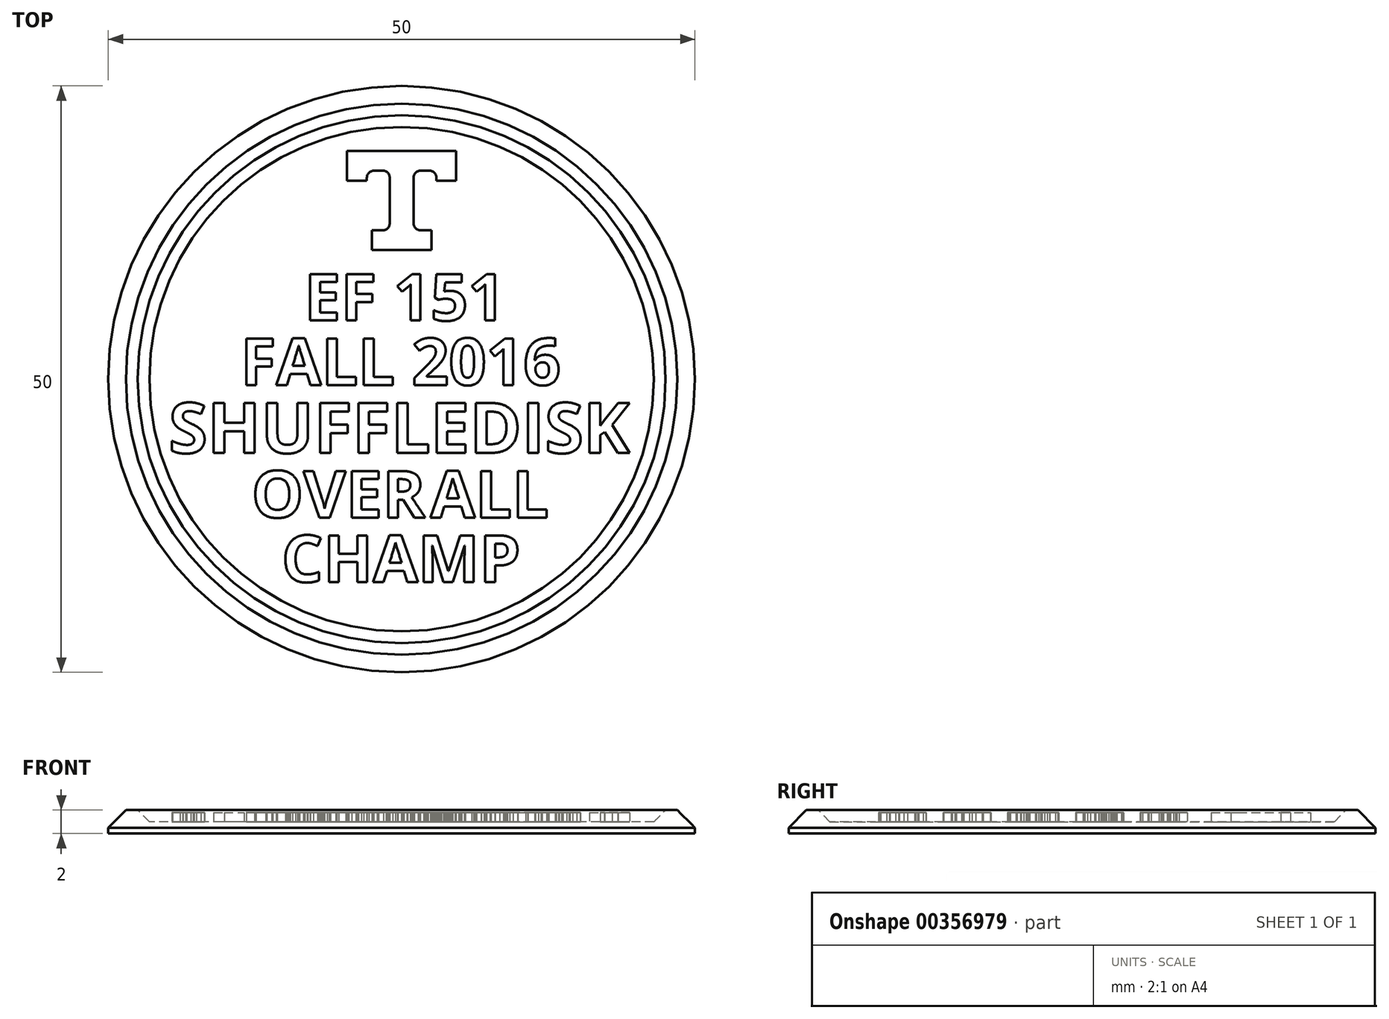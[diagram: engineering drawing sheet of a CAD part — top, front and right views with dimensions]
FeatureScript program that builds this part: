
annotation { "Feature Type Name" : "Feature", "Feature Type Description" : "" }
export const myFeature = defineFeature(function(context is Context, id is Id, definition is map)
    precondition{}
    {
        {
            var Q0;
            Q0=qCreatedBy(makeId("Right.planeOp"),FACE);
            var sketch = newSketch(context, id + "F0", { "sketchPlane" : qUnion([Q0])});
            skLineSegment(sketch, "E0", {"start": v(0, 0) * mm, "end": v(25, 0) * mm});
            skLineSegment(sketch, "E1", {"start": v(25, 0) * mm, "end": v(25, 2) * mm});
            skLineSegment(sketch, "E2", {"start": v(25, 2) * mm, "end": v(0, 2) * mm});
            skLineSegment(sketch, "E3", {"start": v(0, 0) * mm, "end": v(0, 2) * mm});
            skSolve(sketch);
        }
        {
            var Q0;
            Q0=makeQuery(id+"F0.imprint","IMPRINT",FACE,{"disambiguationData":[TD([[makeQuery(id+"F0.imprint","IMPRINT",EDGE,{"derivedFrom":sQuery(id+"F0.wireOp",EDGE,"E0")}),1.0]])]});
            var Q1;
            Q1=sQuery(id+"F0.wireOp",EDGE,"E3");
            revolve(context, id + "F1", {"entities" : qUnion([Q0]), "axis" : qUnion([Q1]), "revolveType" : RevolveType.FULL});
        }
        {
            var Q0;
            Q0=makeQuery(id+"F1.opRevolve","SWEPT_FACE",FACE,{"disambiguationData":[OSD([sQuery(id+"F0.wireOp",EDGE,"E2")])]});
            var sketch = newSketch(context, id + "F2", { "sketchPlane" : qUnion([Q0])});
            skCircle(sketch, "E4", {"center": v(0, 0) * mm, "radius": 22.5 * mm});
            skSolve(sketch);
        }
        {
            var Q0;
            Q0=makeQuery(id+"F2.imprint","IMPRINT",FACE,{"disambiguationData":[TD([[makeQuery(id+"F2.imprint","IMPRINT",EDGE,{"derivedFrom":sQuery(id+"F2.wireOp",EDGE,"E4")}),1.0]])]});
            extrude(context, id + "F3", {"entities" : qUnion([Q0]), "operationType" : NewBodyOperationType.REMOVE, "oppositeDirection" : true, "depth" : 1 * mm, "hasDraft" : true, "draftAngle" : 45 * degree, "draftPullDirection" : true});
        }
        {
            var Q0;
            Q0=makeQuery(id+"F3.boolean.opBoolean","COPY",FACE,{"derivedFrom":makeQuery(id+"F3.opExtrude","CAP_FACE",FACE,{"disambiguationData":[OSD([sQuery(id+"F2.wireOp",EDGE,"E4")])],"isStart":false})});
            var sketch = newSketch(context, id + "F4", { "sketchPlane" : qUnion([Q0])});
            skText(sketch, "E5", { "text": "FALL 2016", "fontName": "OpenSans-Bold.ttf"});
            skText(sketch, "E6", { "text": "SHUFFLEDISK", "fontName": "OpenSans-Bold.ttf"});
            skText(sketch, "E7", { "text": "CHAMP", "fontName": "OpenSans-Bold.ttf"});
            skText(sketch, "E8", { "text": "EF 151", "fontName": "OpenSans-Bold.ttf"});
            skLineSegment(sketch, "E9", {"start": v(-4.66, 16.93) * mm, "end": v(-4.66, 19.47) * mm});
            skLineSegment(sketch, "E10", {"start": v(-4.66, 19.47) * mm, "end": v(0, 19.47) * mm});
            skLineSegment(sketch, "E11", {"start": v(0, 11) * mm, "end": v(-2.54, 11) * mm});
            skLineSegment(sketch, "E12", {"start": v(-2.54, 11) * mm, "end": v(-2.54, 12.7) * mm});
            skLineSegment(sketch, "E13", {"start": v(-2.54, 12.7) * mm, "end": v(-1.6, 12.7) * mm});
            skLineSegment(sketch, "E14", {"start": v(-1.02, 13.29) * mm, "end": v(-1.02, 17.18) * mm});
            skLineSegment(sketch, "E15", {"start": v(-1.6, 17.77) * mm, "end": v(-2.37, 17.77) * mm});
            skLineSegment(sketch, "E16", {"start": v(-2.96, 17.18) * mm, "end": v(-2.96, 16.93) * mm});
            skLineSegment(sketch, "E17", {"start": v(-2.96, 16.93) * mm, "end": v(-4.66, 16.93) * mm});
            skLineSegment(sketch, "E18", {"start": v(0, 19.47) * mm, "end": v(0, 11) * mm});
            skPoint(sketch, "E19.visualSharp", {"position": v(-2.96, 17.77) * mm});
            skArc(sketch, "E19.filletArc", {"start": v(-2.37, 17.77) * mm, "mid": v(-2.79, 17.6) * mm, "end": v(-2.96, 17.18) * mm});
            skPoint(sketch, "E20.visualSharp", {"position": v(-1.02, 17.77) * mm});
            skArc(sketch, "E20.filletArc", {"start": v(-1.02, 17.18) * mm, "mid": v(-1.19, 17.6) * mm, "end": v(-1.6, 17.77) * mm});
            skPoint(sketch, "E21.visualSharp", {"position": v(-1.02, 12.7) * mm});
            skArc(sketch, "E21.filletArc", {"start": v(-1.6, 12.7) * mm, "mid": v(-1.19, 12.87) * mm, "end": v(-1.02, 13.29) * mm});
            skLineSegment(sketch, "E22.MirrorCS", {"start": v(0, 11) * mm, "end": v(2.54, 11) * mm});
            skLineSegment(sketch, "E23.MirrorCS", {"start": v(4.66, 19.47) * mm, "end": v(0, 19.47) * mm});
            skArc(sketch, "E24.MirrorCS", {"start": v(1.6, 12.7) * mm, "mid": v(1.19, 12.87) * mm, "end": v(1.02, 13.29) * mm});
            skArc(sketch, "E25.MirrorCS", {"start": v(1.02, 17.18) * mm, "mid": v(1.19, 17.6) * mm, "end": v(1.6, 17.77) * mm});
            skLineSegment(sketch, "E26.MirrorCS", {"start": v(2.96, 17.18) * mm, "end": v(2.96, 16.93) * mm});
            skArc(sketch, "E27.MirrorCS", {"start": v(2.37, 17.77) * mm, "mid": v(2.79, 17.6) * mm, "end": v(2.96, 17.18) * mm});
            skPoint(sketch, "E28.MirrorP", {"position": v(2.96, 17.77) * mm});
            skPoint(sketch, "E29.MirrorP", {"position": v(1.02, 12.7) * mm});
            skLineSegment(sketch, "E30.MirrorCS", {"start": v(2.54, 11) * mm, "end": v(2.54, 12.7) * mm});
            skPoint(sketch, "E31.MirrorP", {"position": v(1.02, 17.77) * mm});
            skLineSegment(sketch, "E32.MirrorCS", {"start": v(2.54, 12.7) * mm, "end": v(1.6, 12.7) * mm});
            skLineSegment(sketch, "E33.MirrorCS", {"start": v(1.6, 17.77) * mm, "end": v(2.37, 17.77) * mm});
            skLineSegment(sketch, "E34.MirrorCS", {"start": v(4.66, 16.93) * mm, "end": v(4.66, 19.47) * mm});
            skLineSegment(sketch, "E35.MirrorCS", {"start": v(1.02, 13.29) * mm, "end": v(1.02, 17.18) * mm});
            skLineSegment(sketch, "E36.MirrorCS", {"start": v(2.96, 16.93) * mm, "end": v(4.66, 16.93) * mm});
            skText(sketch, "E37", { "text": "OVER", "fontName": "OpenSans-Bold.ttf"});
            skText(sketch, "E38", { "text": "ALL", "fontName": "OpenSans-Bold.ttf"});
            const initialGuessF4  = {"E5": [-0.01374, -0.0005, 1, 0, 0.004], "E6": [-0.01985, -0.0063, 1, 0, 0.0043], "E7": [-0.01023, -0.0173, 1, 0, 0.004], "E8": [-0.0083, 0.005, 1, 0, 0.004], "E37": [-0.01279, -0.0118, 1, 0, 0.004], "E38": [0.00244, -0.0118, 1, 0, 0.004]};
            skSetInitialGuess(sketch, initialGuessF4);
            skSolve(sketch);
        }
        {
            var Q0;
            Q0=makeQuery(id+"F1.opRevolve","SWEPT_EDGE",EDGE,{"disambiguationData":[OSD([sQuery(id+"F0.wireOp",EDGE,"E1"),sQuery(id+"F0.wireOp",EDGE,"E2")])]});
            chamfer(context, id + "F5", {"entities" : qUnion([Q0]), "width" : 1.5 * mm, "tangentPropagation" : true});
        }
        {
            var Q0;
            Q0 = qSketchRegion(id + "F4", true);
            extrude(context, id + "F6", {"entities" : qUnion([Q0]), "operationType" : NewBodyOperationType.ADD, "depth" : .8 * mm});
        }
    });
